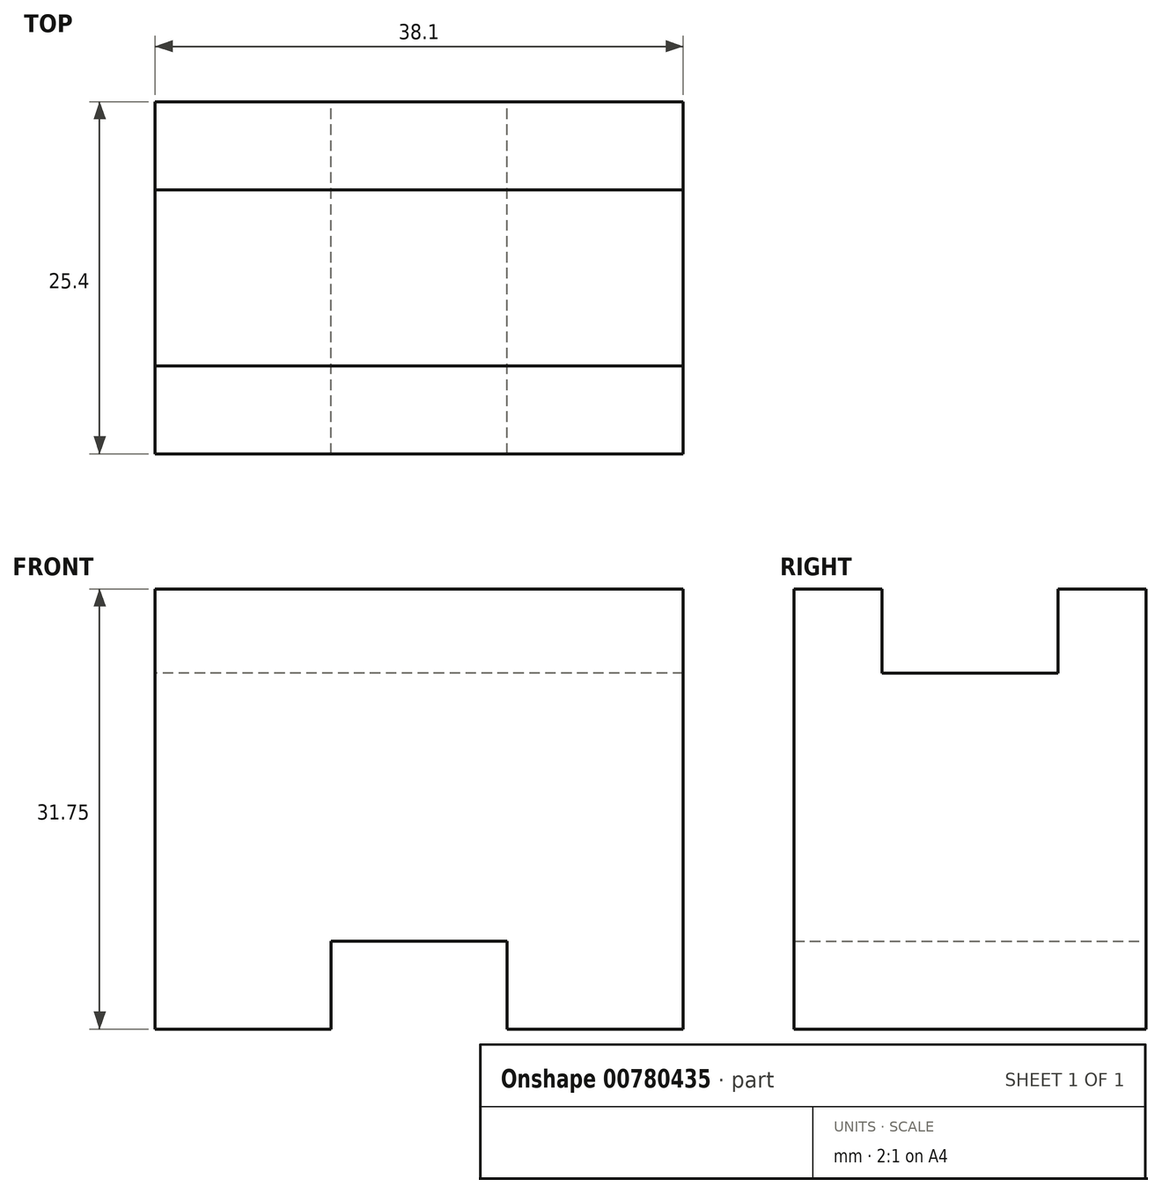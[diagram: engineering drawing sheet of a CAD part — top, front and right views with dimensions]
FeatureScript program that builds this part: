
annotation { "Feature Type Name" : "Feature", "Feature Type Description" : "" }
export const myFeature = defineFeature(function(context is Context, id is Id, definition is map)
    precondition{}
    {
        {
            var Q0;
            Q0=qCreatedBy(makeId("Front.planeOp"),FACE);
            var sketch = newSketch(context, id + "F0", { "sketchPlane" : qUnion([Q0])});
            skLineSegment(sketch, "E0", {"start": v(0, 0) * mm, "end": v(38.1, 0) * mm});
            skLineSegment(sketch, "E1", {"start": v(0, 0) * mm, "end": v(0, 31.75) * mm});
            skLineSegment(sketch, "E2", {"start": v(38.1, 0) * mm, "end": v(38.1, 31.75) * mm});
            skLineSegment(sketch, "E3", {"start": v(38.1, 31.75) * mm, "end": v(0, 31.75) * mm});
            skSolve(sketch);
        }
        {
            var Q0;
            Q0=makeQuery(id+"F0.imprint","IMPRINT",FACE,{"disambiguationData":[TD([[makeQuery(id+"F0.imprint","IMPRINT",EDGE,{"derivedFrom":sQuery(id+"F0.wireOp",EDGE,"E0")}),1.0]])]});
            extrude(context, id + "F1", {"entities" : qUnion([Q0]), "depth" : 25.4 * mm, "offsetDistance" : 25.4 * mm});
        }
        {
            var Q0;
            Q0=qCreatedBy(makeId("Right.planeOp"),FACE);
            var sketch = newSketch(context, id + "F2", { "sketchPlane" : qUnion([Q0])});
            skLineSegment(sketch, "E4", {"start": v(-25.4, 32.03) * mm, "end": v(-19.05, 32.03) * mm});
            skLineSegment(sketch, "E5", {"start": v(-19.05, 32.03) * mm, "end": v(-19.05, 28.9) * mm});
            skLineSegment(sketch, "E6", {"start": v(-19.05, 32.03) * mm, "end": v(-19.05, 25.68) * mm});
            skLineSegment(sketch, "E7", {"start": v(-19.05, 25.68) * mm, "end": v(-6.35, 25.68) * mm});
            skLineSegment(sketch, "E8", {"start": v(-6.35, 25.68) * mm, "end": v(-6.35, 32.03) * mm});
            skLineSegment(sketch, "E9", {"start": v(-6.35, 32.03) * mm, "end": v(0, 32.03) * mm});
            skLineSegment(sketch, "E10", {"start": v(0, 32.03) * mm, "end": v(-19.05, 32.03) * mm});
            skSolve(sketch);
        }
        {
            var Q0;
            Q0 = qSketchRegion(id + "F2", true);
            extrude(context, id + "F3", {"entities" : qUnion([Q0]), "operationType" : NewBodyOperationType.REMOVE, "depth" : 38.1 * mm, "offsetDistance" : 25.4 * mm});
        }
        {
            var Q0;
            Q0=qCreatedBy(makeId("Front.planeOp"),FACE);
            var sketch = newSketch(context, id + "F4", { "sketchPlane" : qUnion([Q0])});
            skLineSegment(sketch, "E11", {"start": v(0, 0) * mm, "end": v(12.7, 0) * mm});
            skLineSegment(sketch, "E12", {"start": v(12.7, 0) * mm, "end": v(12.7, 6.35) * mm});
            skLineSegment(sketch, "E13", {"start": v(12.7, 6.35) * mm, "end": v(25.4, 6.35) * mm});
            skLineSegment(sketch, "E14", {"start": v(25.4, 6.35) * mm, "end": v(25.4, 0) * mm});
            skLineSegment(sketch, "E15", {"start": v(25.4, 0) * mm, "end": v(38.1, 0) * mm});
            skLineSegment(sketch, "E16", {"start": v(12.7, 0) * mm, "end": v(25.4, 0) * mm});
            skSolve(sketch);
        }
        {
            var Q0;
            Q0 = qSketchRegion(id + "F4", true);
            extrude(context, id + "F5", {"entities" : qUnion([Q0]), "operationType" : NewBodyOperationType.REMOVE, "depth" : 25.4 * mm, "offsetDistance" : 25.4 * mm});
        }
    });
